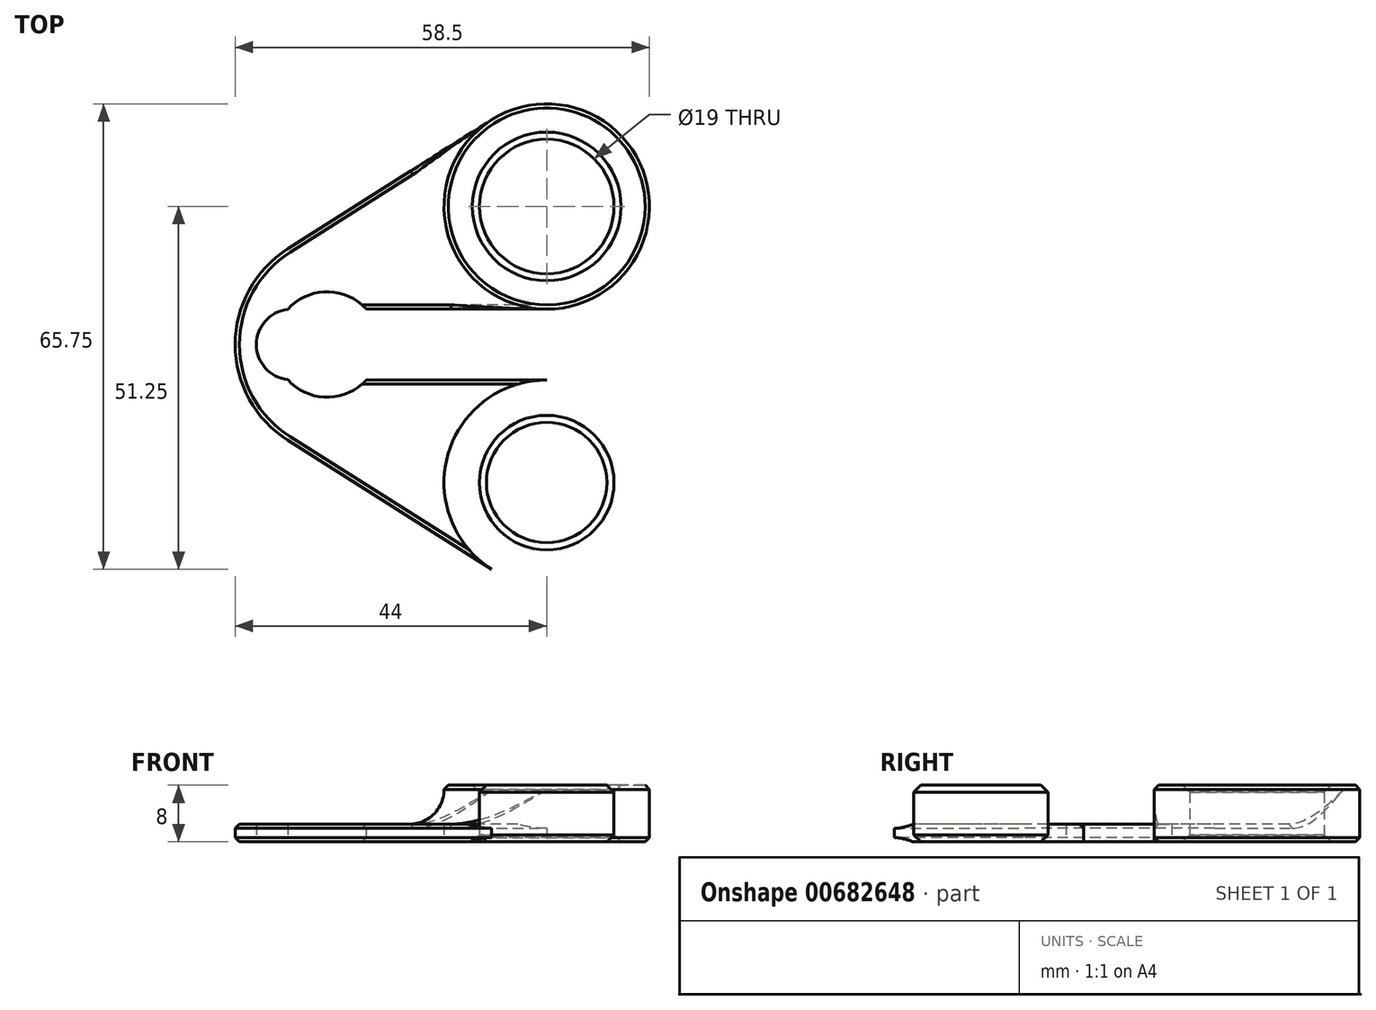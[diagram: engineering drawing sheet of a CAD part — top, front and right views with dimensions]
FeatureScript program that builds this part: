
annotation { "Feature Type Name" : "Feature", "Feature Type Description" : "" }
export const myFeature = defineFeature(function(context is Context, id is Id, definition is map)
    precondition{}
    {
        {
            var Q0;
            Q0=qCreatedBy(makeId("Top.planeOp"),FACE);
            var sketch = newSketch(context, id + "F0", { "sketchPlane" : qUnion([Q0])});
            skCircle(sketch, "E0", {"center": v(0, 0) * mm, "radius": 7.45 * mm});
            skCircle(sketch, "E1", {"center": v(0, 0) * mm, "radius": 15 * mm});
            skCircle(sketch, "E2", {"center": v(31, 19.5) * mm, "radius": 9.5 * mm});
            skCircle(sketch, "E3.0", {"center": v(31, 19.5) * mm, "radius": 14.5 * mm});
            skArc(sketch, "E4", {"start": v(-5.55, 4.97) * mm, "mid": v(-10, 0) * mm, "end": v(-5.55, -4.97) * mm});
            skArc(sketch, "E5", {"start": v(-3.67, 14.54) * mm, "mid": v(-13, 0) * mm, "end": v(-3.67, -14.54) * mm});
            skLineSegment(sketch, "E6", {"start": v(-5.56, 13.52) * mm, "end": v(23.24, 31.75) * mm});
            skLineSegment(sketch, "E7", {"start": v(31, 5) * mm, "end": v(5.52, 5) * mm});
            skLineSegment(sketch, "E8.MirrorCS", {"start": v(-5.56, -13.52) * mm, "end": v(23.24, -31.75) * mm});
            skLineSegment(sketch, "E9.MirrorCS", {"start": v(31, -5) * mm, "end": v(5.52, -5) * mm});
            skCircle(sketch, "E10.MirrorC", {"center": v(31, -19.5) * mm, "radius": 14.5 * mm});
            skCircle(sketch, "E11.MirrorC", {"center": v(31, -19.5) * mm, "radius": 9.5 * mm});
            skSolve(sketch);
        }
        {
            var Q0;
            {var subQ8=sQuery(id+"F0.wireOp",EDGE,"E4");Q0=makeQuery(id+"F0.imprint","IMPRINT",FACE,{"disambiguationData":[TD([[makeQuery(id+"F0.imprint","IMPRINT",EDGE,{"derivedFrom":subQ8}),-1.0]])]});}
            var Q1;
            {var subQ0=sQuery(id+"F0.wireOp",EDGE,"E6");Q1=makeQuery(id+"F0.imprint","IMPRINT",FACE,{"disambiguationData":[TD([[makeQuery(id+"F0.imprint","IMPRINT",EDGE,{"derivedFrom":subQ0}),-1.0]])]});}
            var Q2;
            Q2=makeQuery(id+"F0.imprint","IMPRINT",FACE,{"disambiguationData":[TD([[makeQuery(id+"F0.imprint","IMPRINT",EDGE,{"derivedFrom":sQuery(id+"F0.wireOp",EDGE,"E2")}),-1.0]])]});
            var Q3;
            Q3=makeQuery(id+"F0.imprint","IMPRINT",FACE,{"disambiguationData":[TD([[makeQuery(id+"F0.imprint","IMPRINT",EDGE,{"derivedFrom":sQuery(id+"F0.wireOp",EDGE,"E11.MirrorC")}),1.0]])]});
            var Q4;
            {var subQ0=sQuery(id+"F0.wireOp",EDGE,"E8.MirrorCS");Q4=makeQuery(id+"F0.imprint","IMPRINT",FACE,{"disambiguationData":[TD([[makeQuery(id+"F0.imprint","IMPRINT",EDGE,{"derivedFrom":subQ0}),1.0]])]});}
            var Q5;
            {var subQ3=sQuery(id+"F0.wireOp",EDGE,"E1");var subQ7=makeQuery(id+"F0.imprint","INTERSECT",VERTEX,{"disambiguationData":[OD(0.0)],"derivedFrom":[subQ3,sQuery(id+"F0.wireOp",EDGE,"E5")]});Q5=makeQuery(id+"F0.imprint","IMPRINT",FACE,{"disambiguationData":[TD([[makeQuery(id+"F0.imprint","IMPRINT",EDGE,{"disambiguationData":[TD([[subQ7,1.0]])],"derivedFrom":subQ3}),-1.0]])]});}
            var Q6;
            {var subQ3=sQuery(id+"F0.wireOp",EDGE,"E1");var subQ5=makeQuery(id+"F0.imprint","INTERSECT",VERTEX,{"disambiguationData":[OD(1.0)],"derivedFrom":[subQ3,sQuery(id+"F0.wireOp",EDGE,"E5")]});Q6=makeQuery(id+"F0.imprint","IMPRINT",FACE,{"disambiguationData":[TD([[makeQuery(id+"F0.imprint","IMPRINT",EDGE,{"disambiguationData":[TD([[subQ5,1.0]])],"derivedFrom":subQ3}),-1.0]])]});}
            extrude(context, id + "F1", {"entities" : qUnion([Q0, Q1, Q2, Q3, Q4, Q5, Q6]), "depth" : 2.5 * mm, "offsetDistance" : 25 * mm});
        }
        {
            var Q0;
            Q0=makeQuery(id+"F0.imprint","IMPRINT",FACE,{"disambiguationData":[TD([[makeQuery(id+"F0.imprint","IMPRINT",EDGE,{"derivedFrom":sQuery(id+"F0.wireOp",EDGE,"E11.MirrorC")}),1.0]])]});
            var Q1;
            Q1=makeQuery(id+"F0.imprint","IMPRINT",FACE,{"disambiguationData":[TD([[makeQuery(id+"F0.imprint","IMPRINT",EDGE,{"derivedFrom":sQuery(id+"F0.wireOp",EDGE,"E2")}),-1.0]])]});
            extrude(context, id + "F2", {"entities" : qUnion([Q0, Q1]), "operationType" : NewBodyOperationType.ADD, "depth" : 8 * mm, "offsetDistance" : 25 * mm});
        }
        {
            var Q0;
            {var subQ0=sQuery(id+"F0.wireOp",EDGE,"E3.0");Q0=makeQuery(id+"F2.boolean.opBoolean","INTERSECT",EDGE,{"derivedFrom":[makeQuery(id+"F1.opExtrude","CAP_FACE",FACE,{"disambiguationData":[OSD([sQuery(id+"F0.wireOp",EDGE,"E0"),sQuery(id+"F0.wireOp",EDGE,"E2"),subQ0,sQuery(id+"F0.wireOp",EDGE,"E4"),sQuery(id+"F0.wireOp",EDGE,"E5"),sQuery(id+"F0.wireOp",EDGE,"E6"),sQuery(id+"F0.wireOp",EDGE,"E7"),sQuery(id+"F0.wireOp",EDGE,"E8.MirrorCS"),sQuery(id+"F0.wireOp",EDGE,"E9.MirrorCS"),sQuery(id+"F0.wireOp",EDGE,"E10.MirrorC"),sQuery(id+"F0.wireOp",EDGE,"E11.MirrorC")])],"isStart":false}),makeQuery(id+"F2.opExtrude","SWEPT_FACE",FACE,{"disambiguationData":[OSD([subQ0])]})]});}
            var Q1;
            {var subQ0=sQuery(id+"F0.wireOp",EDGE,"E10.MirrorC");Q1=makeQuery(id+"F2.boolean.opBoolean","INTERSECT",EDGE,{"derivedFrom":[makeQuery(id+"F1.opExtrude","CAP_FACE",FACE,{"disambiguationData":[OSD([sQuery(id+"F0.wireOp",EDGE,"E0"),sQuery(id+"F0.wireOp",EDGE,"E2"),sQuery(id+"F0.wireOp",EDGE,"E3.0"),sQuery(id+"F0.wireOp",EDGE,"E4"),sQuery(id+"F0.wireOp",EDGE,"E5"),sQuery(id+"F0.wireOp",EDGE,"E6"),sQuery(id+"F0.wireOp",EDGE,"E7"),sQuery(id+"F0.wireOp",EDGE,"E8.MirrorCS"),sQuery(id+"F0.wireOp",EDGE,"E9.MirrorCS"),subQ0,sQuery(id+"F0.wireOp",EDGE,"E11.MirrorC")])],"isStart":false}),makeQuery(id+"F2.opExtrude","SWEPT_FACE",FACE,{"disambiguationData":[OSD([subQ0])]})]});}
            fillet(context, id + "F3", {"entities" : qUnion([Q0, Q1]), "radius" : 4.9 * mm, "tangentPropagation" : true, "allowEdgeOverflow" : false});
        }
        {
            var Q0;
            Q0=makeQuery(id+"F1.opExtrude","CAP_EDGE",EDGE,{"disambiguationData":[OSD([sQuery(id+"F0.wireOp",EDGE,"E5")])],"isStart":false});
            var Q1;
            Q1=makeQuery(id+"F1.opExtrude","CAP_EDGE",EDGE,{"disambiguationData":[OSD([sQuery(id+"F0.wireOp",EDGE,"E5")])],"isStart":true});
            var Q2;
            Q2=makeQuery(id+"F2.opExtrude","CAP_EDGE",EDGE,{"disambiguationData":[OSD([sQuery(id+"F0.wireOp",EDGE,"E10.MirrorC")])],"isStart":false});
            var Q3;
            Q3=makeQuery(id+"F2.opExtrude","CAP_EDGE",EDGE,{"disambiguationData":[OSD([sQuery(id+"F0.wireOp",EDGE,"E3.0")])],"isStart":false});
            var Q4;
            Q4=makeQuery(id+"F1.opExtrude","CAP_EDGE",EDGE,{"disambiguationData":[OSD([sQuery(id+"F0.wireOp",EDGE,"E9.MirrorCS")])],"isStart":false});
            var Q5;
            Q5=makeQuery(id+"F1.opExtrude","CAP_EDGE",EDGE,{"disambiguationData":[OSD([sQuery(id+"F0.wireOp",EDGE,"E7")])],"isStart":false});
            chamfer(context, id + "F4", {"entities" : qUnion([Q0, Q1, Q2, Q3, Q4, Q5]), "width" : 0.6 * mm, "tangentPropagation" : true});
        }
        {
            var Q0;
            Q0=makeQuery(id+"F1.opExtrude","CAP_EDGE",EDGE,{"disambiguationData":[OSD([sQuery(id+"F0.wireOp",EDGE,"E11.MirrorC")])],"isStart":true});
            var Q1;
            Q1=makeQuery(id+"F2.opExtrude","CAP_EDGE",EDGE,{"disambiguationData":[OSD([sQuery(id+"F0.wireOp",EDGE,"E11.MirrorC")])],"isStart":false});
            var Q2;
            Q2=makeQuery(id+"F2.opExtrude","CAP_EDGE",EDGE,{"disambiguationData":[OSD([sQuery(id+"F0.wireOp",EDGE,"E2")])],"isStart":false});
            var Q3;
            Q3=makeQuery(id+"F1.opExtrude","CAP_EDGE",EDGE,{"disambiguationData":[OSD([sQuery(id+"F0.wireOp",EDGE,"E2")])],"isStart":true});
            chamfer(context, id + "F5", {"entities" : qUnion([Q0, Q1, Q2, Q3]), "width" : 1 * mm, "tangentPropagation" : true});
        }
    });
